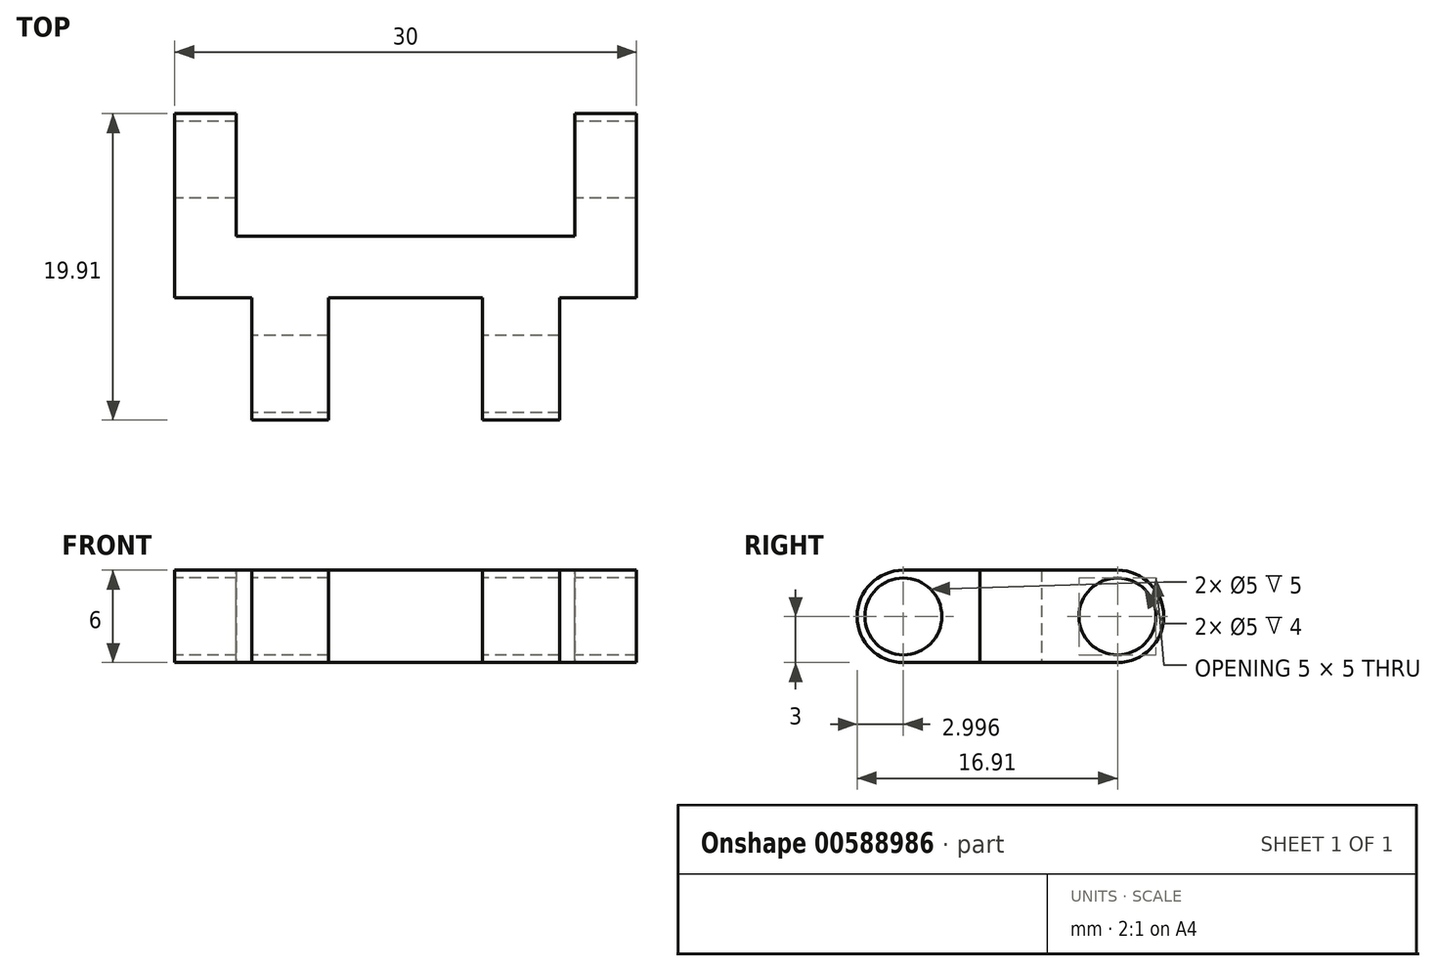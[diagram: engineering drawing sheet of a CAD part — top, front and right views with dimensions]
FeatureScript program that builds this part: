
annotation { "Feature Type Name" : "Feature", "Feature Type Description" : "" }
export const myFeature = defineFeature(function(context is Context, id is Id, definition is map)
    precondition{}
    {
        {
            var Q0;
            Q0=qCreatedBy(makeId("Top.planeOp"),FACE);
            var sketch = newSketch(context, id + "F0", { "sketchPlane" : qUnion([Q0])});
            skLineSegment(sketch, "E0.bottom", {"start": v(15, -10) * mm, "end": v(-15, -10) * mm});
            skLineSegment(sketch, "E0.top", {"start": v(15, 10) * mm, "end": v(-15, 10) * mm});
            skLineSegment(sketch, "E0.left", {"start": v(15, -10) * mm, "end": v(15, 10) * mm});
            skLineSegment(sketch, "E0.right", {"start": v(-15, -10) * mm, "end": v(-15, 10) * mm});
            skPoint(sketch, "E0.middle", {"position": v(0, 0) * mm});
            skLineSegment(sketch, "E1", {"start": v(-11, 10) * mm, "end": v(-11, 2) * mm});
            skLineSegment(sketch, "E2.MirrorCS", {"start": v(11, 10) * mm, "end": v(11, 2) * mm});
            skLineSegment(sketch, "E3", {"start": v(-11, 2) * mm, "end": v(11, 2) * mm});
            skLineSegment(sketch, "E4", {"start": v(-5, -2) * mm, "end": v(5, -2) * mm});
            skLineSegment(sketch, "E5", {"start": v(-5, -2) * mm, "end": v(-5, -10) * mm});
            skLineSegment(sketch, "E6", {"start": v(5, -2) * mm, "end": v(5, -10) * mm});
            skLineSegment(sketch, "E7", {"start": v(-15, -2) * mm, "end": v(-10, -2) * mm});
            skLineSegment(sketch, "E8", {"start": v(-10, -2) * mm, "end": v(-10, -10) * mm});
            skLineSegment(sketch, "E9", {"start": v(15, -2) * mm, "end": v(10, -2) * mm});
            skLineSegment(sketch, "E10", {"start": v(10, -2) * mm, "end": v(10, -10) * mm});
            skSolve(sketch);
        }
        {
            var Q0;
            {var subQ8=sQuery(id+"F0.wireOp",EDGE,"E1");Q0=makeQuery(id+"F0.imprint","IMPRINT",FACE,{"disambiguationData":[TD([[makeQuery(id+"F0.imprint","IMPRINT",EDGE,{"derivedFrom":subQ8}),-1.0]])]});}
            extrude(context, id + "F1", {"entities" : qUnion([Q0]), "depth" : 6 * mm, "offsetDistance" : 25 * mm});
        }
        {
            var Q0;
            Q0=makeQuery(id+"F1.opExtrude","SWEPT_FACE",FACE,{"disambiguationData":[OSD([sQuery(id+"F0.wireOp",EDGE,"E0.right")])]});
            var sketch = newSketch(context, id + "F2", { "sketchPlane" : qUnion([Q0])});
            skCircle(sketch, "E11", {"center": v(-6.95, 3) * mm, "radius": 3 * mm});
            skPoint(sketch, "E11.centerSnap0", {"position": v(-10, 3) * mm});
            skCircle(sketch, "E12", {"center": v(-6.95, 3) * mm, "radius": 2.5 * mm});
            skCircle(sketch, "E13", {"center": v(6.96, 3) * mm, "radius": 3 * mm});
            skPoint(sketch, "E13.centerSnap0", {"position": v(10, 3) * mm});
            skCircle(sketch, "E14", {"center": v(6.96, 3) * mm, "radius": 2.5 * mm});
            skLineSegment(sketch, "E15.0.0", {"start": v(2, 0) * mm, "end": v(10, 0) * mm});
            skLineSegment(sketch, "E15.0.1", {"start": v(10, 0) * mm, "end": v(10, 6) * mm});
            skLineSegment(sketch, "E15.0.2", {"start": v(10, 6) * mm, "end": v(2, 6) * mm});
            skLineSegment(sketch, "E15.0.3", {"start": v(2, 6) * mm, "end": v(2, 0) * mm});
            skSolve(sketch);
        }
        {
            var Q0;
            Q0=makeQuery(id+"F2.imprint","IMPRINT",FACE,{"disambiguationData":[TD([[makeQuery(id+"F2.imprint","IMPRINT",EDGE,{"derivedFrom":sQuery(id+"F2.wireOp",EDGE,"E12")}),1.0]])]});
            var Q1;
            {var subQ1=sQuery(id+"F0.wireOp",EDGE,"E0.right");var subQ6=makeQuery(id+"F1.opExtrude","SWEPT_EDGE",EDGE,{"disambiguationData":[OSD([sQuery(id+"F0.wireOp",EDGE,"E0.top"),subQ1])]});Q1=makeQuery(id+"F2.imprint","IMPRINT",FACE,{"disambiguationData":[TD([[makeQuery(id+"F2.imprint","IMPRINT",EDGE,{"derivedFrom":subQ6}),1.0]])]});}
            var Q2;
            Q2=makeQuery(id+"F2.imprint","IMPRINT",FACE,{"disambiguationData":[TD([[makeQuery(id+"F2.imprint","IMPRINT",EDGE,{"derivedFrom":sQuery(id+"F2.wireOp",EDGE,"E14")}),1.0]])]});
            var Q3;
            {var subQ5=sQuery(id+"F2.wireOp",EDGE,"E15.0.1");Q3=makeQuery(id+"F2.imprint","IMPRINT",FACE,{"disambiguationData":[TD([[makeQuery(id+"F2.imprint","IMPRINT",EDGE,{"derivedFrom":subQ5}),1.0]])]});}
            extrude(context, id + "F3", {"entities" : qUnion([Q0, Q1, Q2, Q3]), "operationType" : NewBodyOperationType.REMOVE, "oppositeDirection" : true, "depth" : 50 * mm, "offsetDistance" : 25 * mm});
        }
    });
